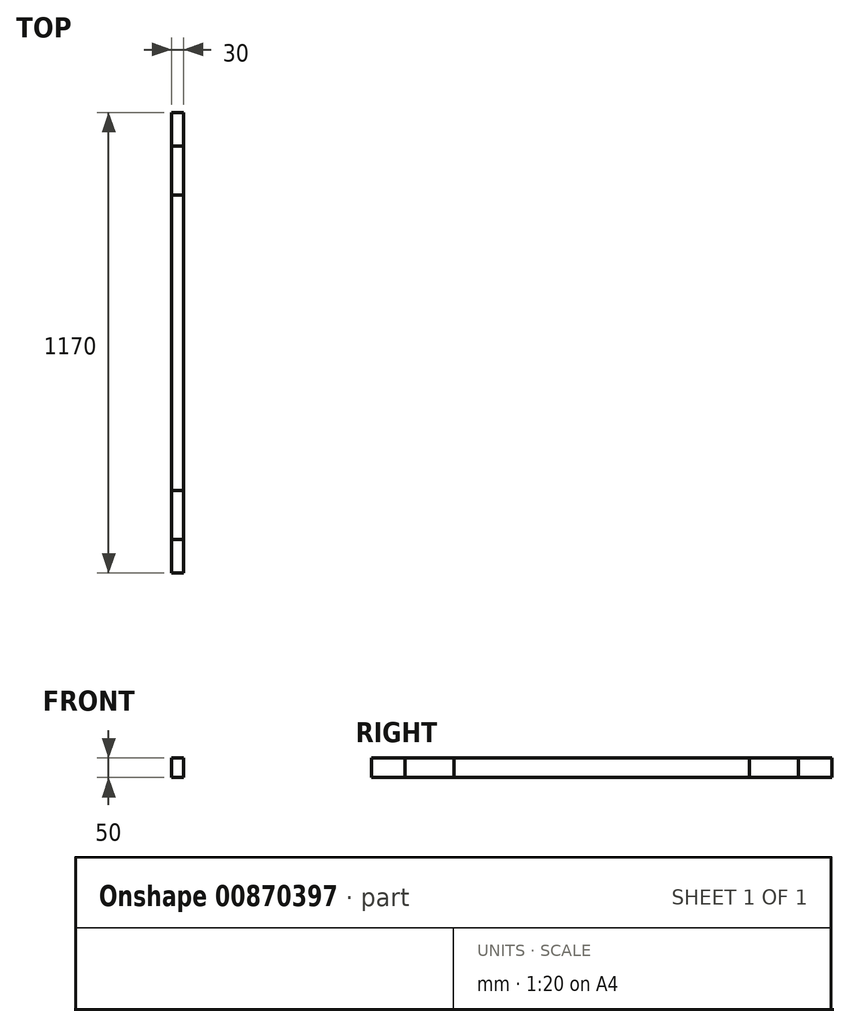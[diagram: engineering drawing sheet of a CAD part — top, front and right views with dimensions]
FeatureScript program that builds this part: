
annotation { "Feature Type Name" : "Feature", "Feature Type Description" : "" }
export const myFeature = defineFeature(function(context is Context, id is Id, definition is map)
    precondition{}
    {
        {
            var Q0;
            Q0=qCreatedBy(makeId("Front.planeOp"),FACE);
            var sketch = newSketch(context, id + "F0", { "sketchPlane" : qUnion([Q0])});
            skLineSegment(sketch, "E0.bottom", {"start": v(-13.92, 25.47) * mm, "end": v(16.08, 25.47) * mm});
            skLineSegment(sketch, "E0.top", {"start": v(-13.92, -24.53) * mm, "end": v(16.08, -24.53) * mm});
            skLineSegment(sketch, "E0.left", {"start": v(-13.92, 25.47) * mm, "end": v(-13.92, -24.53) * mm});
            skLineSegment(sketch, "E0.right", {"start": v(16.08, 25.47) * mm, "end": v(16.08, -24.53) * mm});
            skSolve(sketch);
        }
        {
            var Q0;
            Q0=makeQuery(id+"F0.imprint","IMPRINT",FACE,{"disambiguationData":[TD([[makeQuery(id+"F0.imprint","IMPRINT",EDGE,{"derivedFrom":sQuery(id+"F0.wireOp",EDGE,"E0.bottom")}),-1.0]])]});
            extrude(context, id + "F1", {"entities" : qUnion([Q0]), "endBound" : BoundingType.SYMMETRIC, "depth" : 1170 * mm, "offsetDistance" : 25 * mm});
        }
        {
            var Q0;
            Q0 = qSketchRegion(id + "F0", true);
            extrude(context, id + "F2", {"entities" : qUnion([Q0]), "endBound" : BoundingType.SYMMETRIC, "depth" : 1000 * mm, "offsetDistance" : 25 * mm});
        }
        {
            var Q0;
            Q0 = qSketchRegion(id + "F0", true);
            extrude(context, id + "F3", {"entities" : qUnion([Q0]), "endBound" : BoundingType.SYMMETRIC, "depth" : 750 * mm, "offsetDistance" : 25 * mm});
        }
    });
